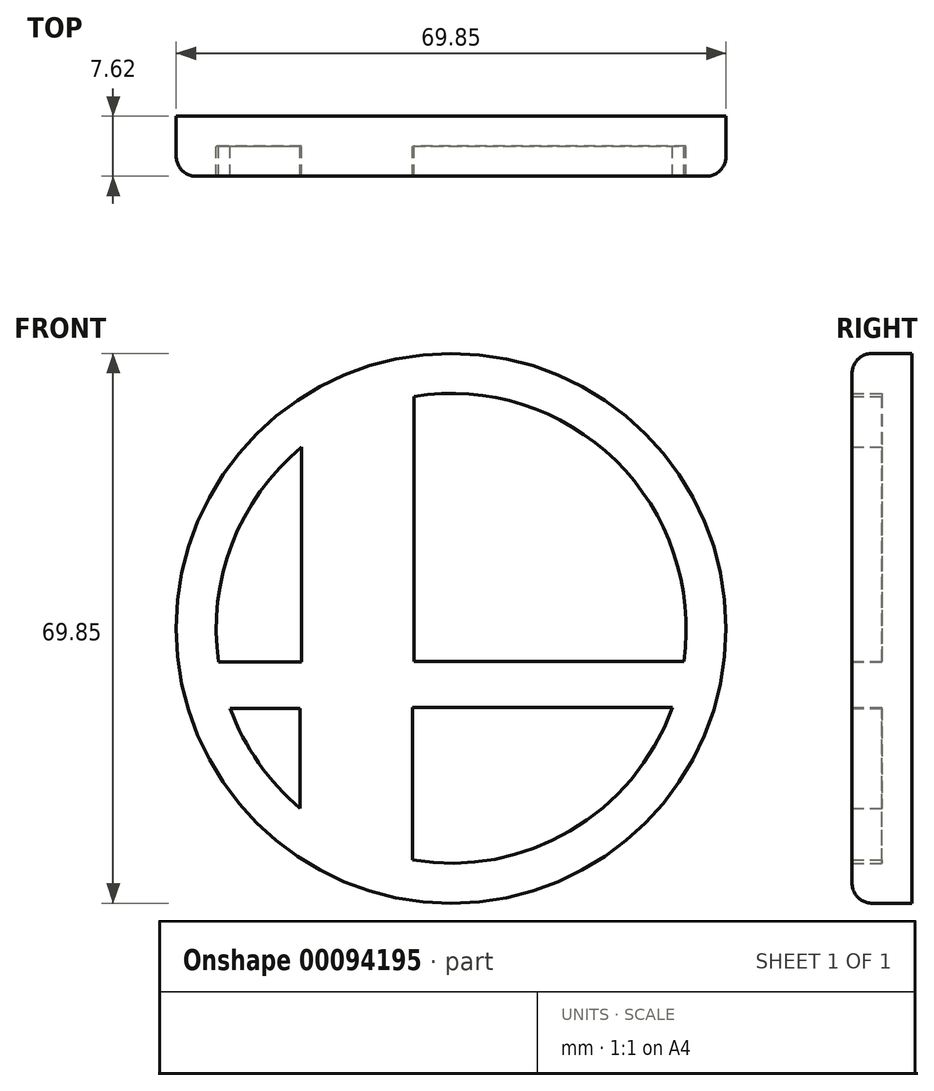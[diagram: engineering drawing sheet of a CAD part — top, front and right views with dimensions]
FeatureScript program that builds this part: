
annotation { "Feature Type Name" : "Feature", "Feature Type Description" : "" }
export const myFeature = defineFeature(function(context is Context, id is Id, definition is map)
    precondition{}
    {
        {
            var Q0;
            Q0=qCreatedBy(makeId("Front.planeOp"),FACE);
            var sketch = newSketch(context, id + "F0", { "sketchPlane" : qUnion([Q0])});
            skLineSegment(sketch, "E0", {"start": v(0, 0) * mm, "end": v(31.75, 0) * mm});
            skCircle(sketch, "E1", {"center": v(31.4, 32.14) * mm, "radius": 34.93 * mm});
            skCircle(sketch, "E2", {"center": v(31.4, 32.14) * mm, "radius": 29.85 * mm});
            skLineSegment(sketch, "E3", {"start": v(1.87, 27.85) * mm, "end": v(12.4, 27.85) * mm});
            skLineSegment(sketch, "E4", {"start": v(12.4, 27.85) * mm, "end": v(12.4, 55.15) * mm});
            skLineSegment(sketch, "E5", {"start": v(26.67, 61.6) * mm, "end": v(26.67, 27.95) * mm});
            skLineSegment(sketch, "E6", {"start": v(26.67, 27.95) * mm, "end": v(60.96, 27.95) * mm});
            skLineSegment(sketch, "E7", {"start": v(3.35, 21.96) * mm, "end": v(12.24, 21.96) * mm});
            skLineSegment(sketch, "E8", {"start": v(12.24, 21.96) * mm, "end": v(12.24, 9.26) * mm});
            skLineSegment(sketch, "E9", {"start": v(26.48, 2.7) * mm, "end": v(26.48, 22.06) * mm});
            skLineSegment(sketch, "E10", {"start": v(26.48, 22.06) * mm, "end": v(59.5, 22.06) * mm});
            skSolve(sketch);
        }
        {
            var Q0;
            Q0=makeQuery(id+"F0.imprint","IMPRINT",FACE,{"disambiguationData":[TD([[makeQuery(id+"F0.imprint","IMPRINT",EDGE,{"derivedFrom":sQuery(id+"F0.wireOp",EDGE,"E1")}),1.0]])]});
            var Q1;
            {var subQ2=sQuery(id+"F0.wireOp",EDGE,"E3");Q1=makeQuery(id+"F0.imprint","IMPRINT",FACE,{"disambiguationData":[TD([[makeQuery(id+"F0.imprint","IMPRINT",EDGE,{"derivedFrom":subQ2}),-1.0]])]});}
            extrude(context, id + "F1", {"entities" : qUnion([Q0, Q1]), "depth" : 7.62 * mm});
        }
        {
            var Q0;
            {var subQ0=sQuery(id+"F0.wireOp",EDGE,"E3");Q0=makeQuery(id+"F0.imprint","IMPRINT",FACE,{"disambiguationData":[TD([[makeQuery(id+"F0.imprint","IMPRINT",EDGE,{"derivedFrom":subQ0}),1.0]])]});}
            var Q1;
            {var subQ0=sQuery(id+"F0.wireOp",EDGE,"E5");Q1=makeQuery(id+"F0.imprint","IMPRINT",FACE,{"disambiguationData":[TD([[makeQuery(id+"F0.imprint","IMPRINT",EDGE,{"derivedFrom":subQ0}),1.0]])]});}
            var Q2;
            {var subQ0=sQuery(id+"F0.wireOp",EDGE,"E9");Q2=makeQuery(id+"F0.imprint","IMPRINT",FACE,{"disambiguationData":[TD([[makeQuery(id+"F0.imprint","IMPRINT",EDGE,{"derivedFrom":subQ0}),-1.0]])]});}
            var Q3;
            {var subQ0=sQuery(id+"F0.wireOp",EDGE,"E7");Q3=makeQuery(id+"F0.imprint","IMPRINT",FACE,{"disambiguationData":[TD([[makeQuery(id+"F0.imprint","IMPRINT",EDGE,{"derivedFrom":subQ0}),-1.0]])]});}
            extrude(context, id + "F2", {"entities" : qUnion([Q0, Q1, Q2, Q3]), "operationType" : NewBodyOperationType.ADD, "depth" : 3.8 * mm});
        }
        {
            var Q0;
            Q0=makeQuery(id+"F1.opExtrude","CAP_EDGE",EDGE,{"disambiguationData":[OSD([sQuery(id+"F0.wireOp",EDGE,"E1")])],"isStart":false});
            fillet(context, id + "F3", {"entities" : qUnion([Q0]), "radius" : 2.54 * mm, "tangentPropagation" : true, "allowEdgeOverflow" : false});
        }
    });
